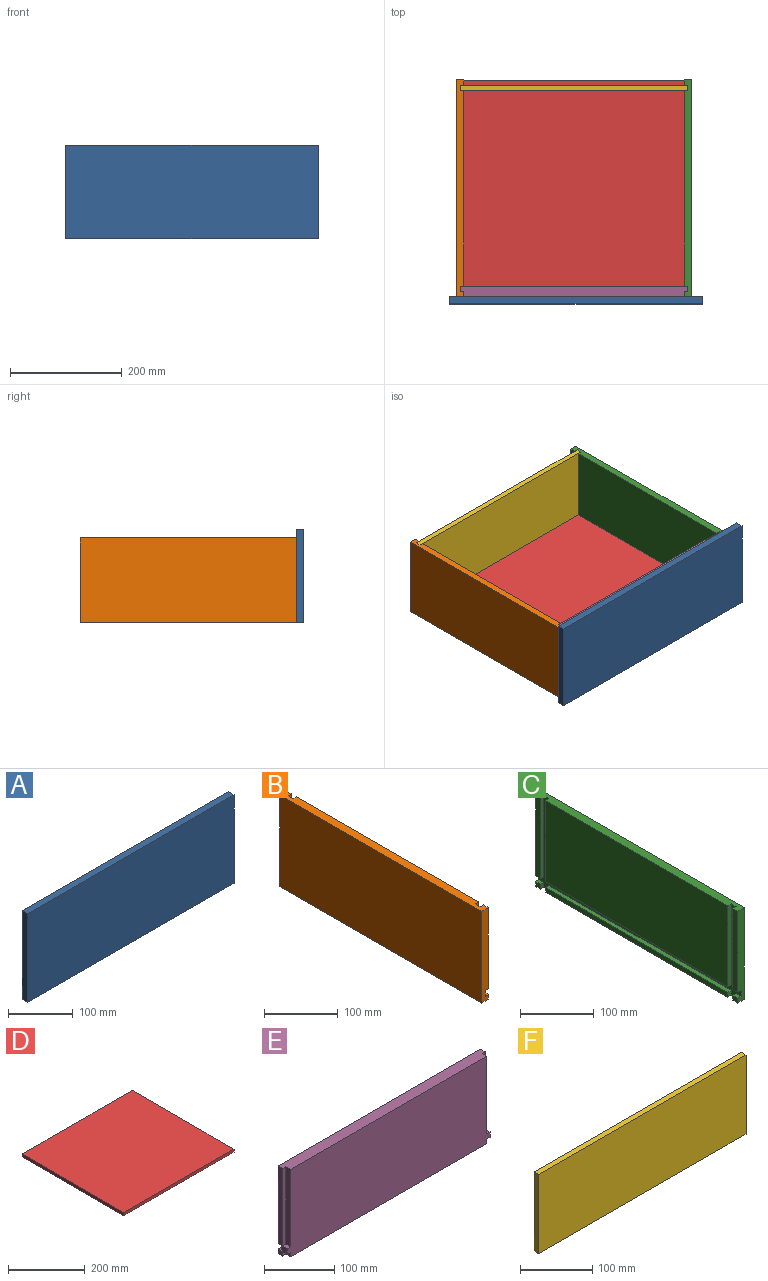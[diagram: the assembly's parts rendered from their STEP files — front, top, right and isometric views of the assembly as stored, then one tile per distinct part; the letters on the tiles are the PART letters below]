
ASSEMBLY  parts=6 mates=5
PART A: 6 faces, bbox 451.6x12.7x167.7 mm
  f0: plane 167.74x12.7mm, normal (1,0,0), area 2130.3mm2, adj f1,f3,f4,f5
  f1: plane 451.64x12.7mm, normal (0,0,1), area 5735.8mm2, adj f0,f2,f4,f5
  f2: plane 167.74x12.7mm, normal (-1,0,0), area 2130.3mm2, adj f1,f3,f4,f5
  f3: plane 451.64x12.7mm, normal (0,0,-1), area 5735.8mm2, adj f0,f2,f4,f5
  f4: plane 451.64x167.74mm, normal (0,-1,0), area 75758.4mm2, adj f0,f1,f2,f3
  f5: plane 451.64x167.74mm, normal (0,1,0), area 75758.4mm2, adj f0,f1,f2,f3
PART B: 26 faces, bbox 12.7x387.4x151.9 mm
  f0: plane 9.53x7.92mm, normal (1,0,0), area 75.5mm2, adj f3,f11,f14,f23
  f1: plane 134.42x9.53mm, normal (1,0,0), area 1280.3mm2, adj f2,f4,f14,f24
  f2: plane 387.35x12.7mm, normal (0,0,1), area 4798.4mm2, adj f1,f6,f9,f12,f13,f14,f17,f18
  f3: plane 9.53x6.35mm, normal (0,0,1), area 60.5mm2, adj f0,f14,f17,f23
  f4: plane 9.53x6.35mm, normal (0,0,-1), area 60.5mm2, adj f1,f14,f17,f24
  f5: plane 349.25x7.92mm, normal (1,0,0), area 2767.7mm2, adj f7,f11,f21,f22
  f6: plane 349.25x134.42mm, normal (1,0,0), area 46945.1mm2, adj f2,f8,f18,f25
  f7: plane 349.25x6.35mm, normal (0,0,1), area 2217.7mm2, adj f5,f17,f21,f22
  f8: plane 349.25x6.35mm, normal (0,0,-1), area 2217.7mm2, adj f6,f17,f18,f25
  f9: plane 151.87x12.7mm, normal (0,1,0), area 1868.2mm2, adj f2,f10,f11,f12,f13,f15,f16,f17
  f10: plane 9.53x7.92mm, normal (1,0,0), area 75.5mm2, adj f9,f11,f15,f20
  f11: plane 387.35x12.7mm, normal (0,0,-1), area 4798.4mm2, adj f0,f5,f9,f10,f12,f14,f17,f20
  f12: plane 387.35x151.87mm, normal (-1,0,0), area 58825.5mm2, adj f2,f9,f11,f14
  f13: plane 134.42x9.53mm, normal (1,0,0), area 1280.3mm2, adj f2,f9,f16,f19
  f14: plane 151.87x12.7mm, normal (0,-1,0), area 1868.2mm2, adj f0,f1,f2,f3,f4,f11,f12,f17
  f15: plane 9.53x6.35mm, normal (0,0,1), area 60.5mm2, adj f9,f10,f17,f20
  f16: plane 9.53x6.35mm, normal (0,0,-1), area 60.5mm2, adj f9,f13,f17,f19
  f17: plane 387.35x151.87mm, normal (1,0,0), area 6401.1mm2, adj f2,f3,f4,f7,f8,f9,f11,f14
  f18: plane 134.42x6.35mm, normal (0,1,0), area 853.5mm2, adj f2,f6,f8,f17
  f19: plane 134.42x6.35mm, normal (0,-1,0), area 853.5mm2, adj f2,f13,f16,f17
  f20: plane 7.92x6.35mm, normal (0,-1,0), area 50.3mm2, adj f10,f11,f15,f17
  f21: plane 7.92x6.35mm, normal (0,1,0), area 50.3mm2, adj f5,f7,f11,f17
  f22: plane 7.92x6.35mm, normal (0,-1,0), area 50.3mm2, adj f5,f7,f11,f17
  f23: plane 7.92x6.35mm, normal (0,1,0), area 50.3mm2, adj f0,f3,f11,f17
  f24: plane 134.42x6.35mm, normal (0,1,0), area 853.5mm2, adj f1,f2,f4,f17
  f25: plane 134.42x6.35mm, normal (0,-1,0), area 853.5mm2, adj f2,f6,f8,f17
PART C: 26 faces, bbox 12.7x387.4x151.9 mm
  f0: plane 9.53x7.92mm, normal (-1,0,0), area 75.5mm2, adj f3,f11,f14,f23
  f1: plane 134.42x9.53mm, normal (-1,0,0), area 1280.3mm2, adj f2,f4,f14,f24
  f2: plane 387.35x12.7mm, normal (0,0,1), area 4798.4mm2, adj f1,f6,f9,f12,f13,f14,f17,f18
  f3: plane 9.53x6.35mm, normal (0,0,1), area 60.5mm2, adj f0,f14,f17,f23
  f4: plane 9.53x6.35mm, normal (0,0,-1), area 60.5mm2, adj f1,f14,f17,f24
  f5: plane 349.25x7.92mm, normal (-1,0,0), area 2767.7mm2, adj f7,f11,f21,f22
  f6: plane 349.25x134.42mm, normal (-1,0,0), area 46945.1mm2, adj f2,f8,f18,f25
  f7: plane 349.25x6.35mm, normal (0,0,1), area 2217.7mm2, adj f5,f17,f21,f22
  f8: plane 349.25x6.35mm, normal (0,0,-1), area 2217.7mm2, adj f6,f17,f18,f25
  f9: plane 151.87x12.7mm, normal (0,1,0), area 1868.2mm2, adj f2,f10,f11,f12,f13,f15,f16,f17
  f10: plane 9.53x7.92mm, normal (-1,0,0), area 75.5mm2, adj f9,f11,f15,f20
  f11: plane 387.35x12.7mm, normal (0,0,-1), area 4798.4mm2, adj f0,f5,f9,f10,f12,f14,f17,f20
  f12: plane 387.35x151.87mm, normal (1,0,0), area 58825.5mm2, adj f2,f9,f11,f14
  f13: plane 134.42x9.53mm, normal (-1,0,0), area 1280.3mm2, adj f2,f9,f16,f19
  f14: plane 151.87x12.7mm, normal (0,-1,0), area 1868.2mm2, adj f0,f1,f2,f3,f4,f11,f12,f17
  f15: plane 9.53x6.35mm, normal (0,0,1), area 60.5mm2, adj f9,f10,f17,f20
  f16: plane 9.53x6.35mm, normal (0,0,-1), area 60.5mm2, adj f9,f13,f17,f19
  f17: plane 387.35x151.87mm, normal (-1,0,0), area 6401.1mm2, adj f2,f3,f4,f7,f8,f9,f11,f14
  f18: plane 134.42x6.35mm, normal (0,1,0), area 853.5mm2, adj f2,f6,f8,f17
  f19: plane 134.42x6.35mm, normal (0,-1,0), area 853.5mm2, adj f2,f13,f16,f17
  f20: plane 7.92x6.35mm, normal (0,-1,0), area 50.3mm2, adj f10,f11,f15,f17
  f21: plane 7.92x6.35mm, normal (0,1,0), area 50.3mm2, adj f5,f7,f11,f17
  f22: plane 7.92x6.35mm, normal (0,-1,0), area 50.3mm2, adj f5,f7,f11,f17
  f23: plane 7.92x6.35mm, normal (0,1,0), area 50.3mm2, adj f0,f3,f11,f17
  f24: plane 134.42x6.35mm, normal (0,1,0), area 853.5mm2, adj f1,f2,f4,f17
  f25: plane 134.42x6.35mm, normal (0,-1,0), area 853.5mm2, adj f2,f6,f8,f17
PART D: 6 faces, bbox 406.4x376.2x9.5 mm
  f0: plane 376.22x9.53mm, normal (1,0,0), area 3583.5mm2, adj f1,f2,f3,f4
  f1: plane 406.4x9.53mm, normal (0,1,0), area 3871mm2, adj f0,f3,f4,f5
  f2: plane 406.4x9.53mm, normal (0,-1,0), area 3871mm2, adj f0,f3,f4,f5
  f3: plane 406.4x376.22mm, normal (0,0,-1), area 152897.8mm2, adj f0,f1,f2,f5
  f4: plane 406.4x376.22mm, normal (0,0,1), area 152897.8mm2, adj f0,f1,f2,f5
  f5: plane 376.22x9.53mm, normal (-1,0,0), area 3583.5mm2, adj f1,f2,f3,f4
PART E: 22 faces, bbox 406.4x19.1x151.9 mm
  f0: plane 9.53x7.92mm, normal (1,0,0), area 75.5mm2, adj f1,f2,f11,f12
  f1: plane 9.53x6.35mm, normal (0,0,-1), area 60.5mm2, adj f0,f2,f3,f11
  f2: plane 7.92x6.35mm, normal (0,-1,0), area 50.3mm2, adj f0,f1,f3,f12
  f3: plane 151.87x19.05mm, normal (1,0,0), area 1461.8mm2, adj f1,f2,f4,f5,f7,f8,f9,f10
  f4: plane 9.53x6.35mm, normal (0,0,1), area 60.5mm2, adj f3,f5,f6,f11
  f5: plane 134.42x6.35mm, normal (0,-1,0), area 853.5mm2, adj f3,f4,f6,f10
  f6: plane 134.42x9.53mm, normal (1,0,0), area 1280.3mm2, adj f4,f5,f10,f11
  f7: plane 406.4x7.92mm, normal (0,0,1), area 3220.6mm2, adj f3,f8,f13,f18
  f8: plane 406.4x9.53mm, normal (0,1,0), area 3871mm2, adj f3,f7,f9,f18
  f9: plane 406.4x7.92mm, normal (0,0,-1), area 3220.6mm2, adj f3,f8,f14,f18
  f10: plane 406.4x19.05mm, normal (0,0,1), area 7621mm2, adj f3,f5,f6,f11,f14,f18,f20,f21
  f11: plane 406.4x151.87mm, normal (0,-1,0), area 59910.8mm2, adj f0,f1,f3,f4,f6,f10,f12,f15
  f12: plane 406.4x19.05mm, normal (0,0,-1), area 7621mm2, adj f0,f2,f3,f11,f13,f15,f17,f18
  f13: plane 406.4x7.92mm, normal (0,1,0), area 3220.6mm2, adj f3,f7,f12,f18
  f14: plane 406.4x134.42mm, normal (0,1,0), area 54627mm2, adj f3,f9,f10,f18
  f15: plane 9.53x7.92mm, normal (-1,0,0), area 75.5mm2, adj f11,f12,f16,f17
  f16: plane 9.53x6.35mm, normal (0,0,-1), area 60.5mm2, adj f11,f15,f17,f18
  f17: plane 7.92x6.35mm, normal (0,-1,0), area 50.3mm2, adj f12,f15,f16,f18
  f18: plane 151.87x19.05mm, normal (-1,0,0), area 1461.8mm2, adj f7,f8,f9,f10,f11,f12,f13,f14
  f19: plane 9.53x6.35mm, normal (0,0,1), area 60.5mm2, adj f11,f18,f20,f21
  f20: plane 134.42x6.35mm, normal (0,-1,0), area 853.5mm2, adj f10,f18,f19,f21
  f21: plane 134.42x9.53mm, normal (-1,0,0), area 1280.3mm2, adj f10,f11,f19,f20
PART F: 6 faces, bbox 406.4x9.5x134.4 mm
  f0: plane 134.42x9.53mm, normal (1,0,0), area 1280.3mm2, adj f1,f2,f3,f4
  f1: plane 406.4x9.53mm, normal (0,0,-1), area 3871mm2, adj f0,f3,f4,f5
  f2: plane 406.4x9.53mm, normal (0,0,1), area 3871mm2, adj f0,f3,f4,f5
  f3: plane 406.4x134.42mm, normal (0,-1,0), area 54627mm2, adj f0,f1,f2,f5
  f4: plane 406.4x134.42mm, normal (0,1,0), area 54627mm2, adj f0,f1,f2,f5
  f5: plane 134.42x9.53mm, normal (-1,0,0), area 1280.3mm2, adj f1,f2,f3,f4
PLACE A t=(-1.6,0,0)mm
PLACE B at identity fixed
PLACE C at identity
PLACE D at identity
PLACE E at identity
PLACE F at identity
MATE fastened B.f11 <-> A.f3  axis (0,0,-1) through (-698.5,-406.4,402.16)mm
MATE fastened F.f2 <-> C.f2  axis (0,0,1) through (-285.75,-38.1,554.02)mm
MATE fastened D.f1 <-> C.f9  axis (0,1,0) through (-285.75,-19.05,419.61)mm
MATE fastened F.f2 <-> B.f2  axis (0,0,1) through (-692.15,-38.1,554.02)mm
MATE fastened C.f2 <-> E.f10  axis (0,0,1) through (-292.1,-406.4,554.02)mm
